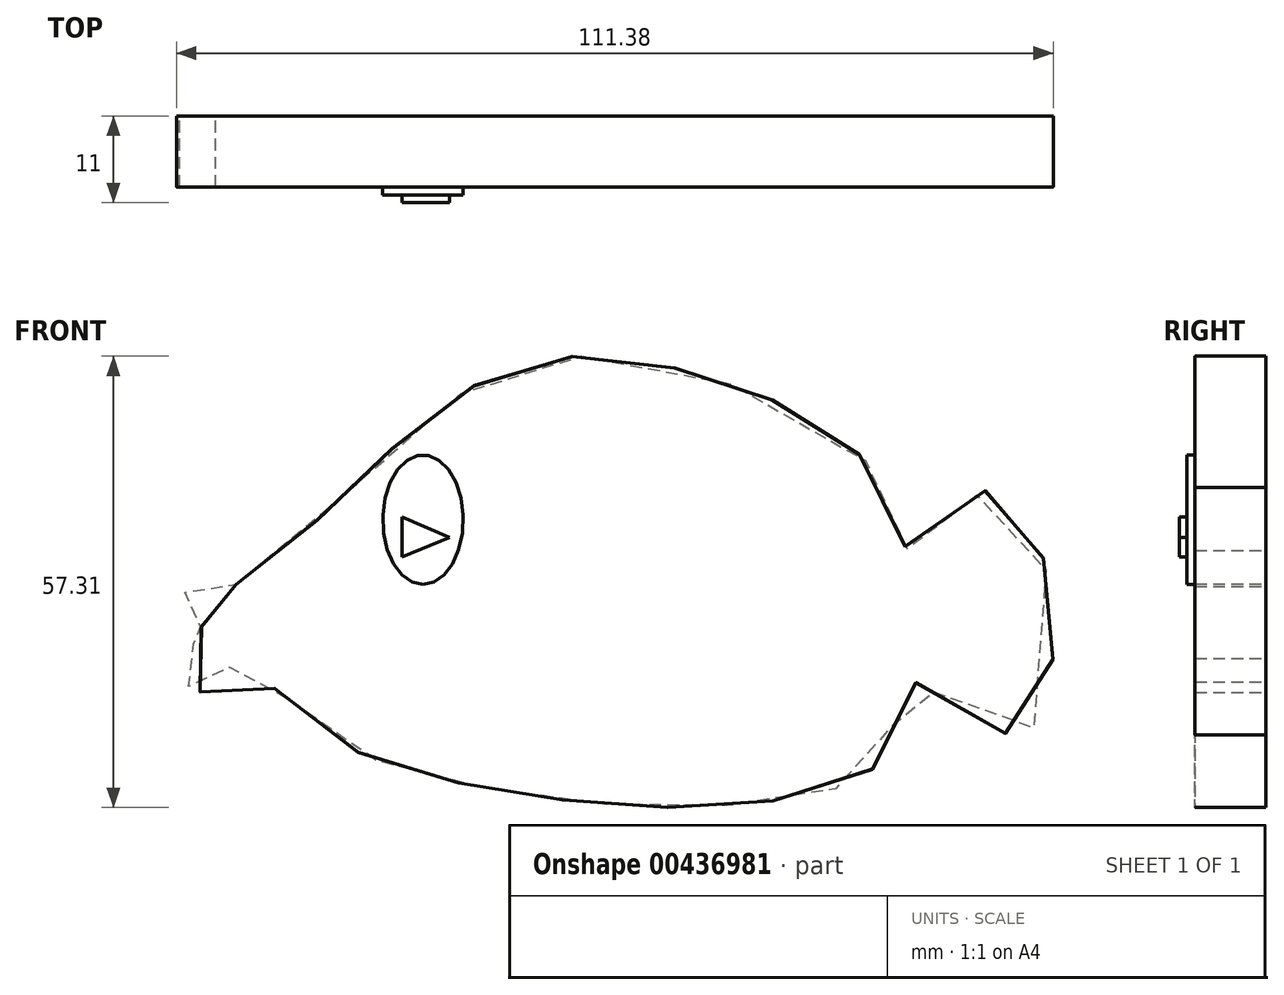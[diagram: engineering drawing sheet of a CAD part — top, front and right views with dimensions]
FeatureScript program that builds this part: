
annotation { "Feature Type Name" : "Feature", "Feature Type Description" : "" }
export const myFeature = defineFeature(function(context is Context, id is Id, definition is map)
    precondition{}
    {
        {
            var Q0;
            Q0=qCreatedBy(makeId("Front.planeOp"),FACE);
            var sketch = newSketch(context, id + "F0", { "sketchPlane" : qUnion([Q0])});
            skFitSpline(sketch, "E0", {"points": [v(-50.37, 0) * mm, v(-24.75, 22.16) * mm, v(0, 28.5) * mm, v(31.66, 12.95) * mm, v(35.69, 4.32) * mm, v(47.49, 12.09) * mm, v(50.37, -18.7) * mm, v(35.11, -12.38) * mm, v(32.23, -21) * mm, v(21, -27.05) * mm, v(0, -28.2) * mm, v(-23.02, -25.04) * mm, v(-40, -18.13) * mm, v(-50.65, -9.5) * mm, v(-52.1, -12.95) * mm, v(-56.4, -12.95) * mm, v(-57.27, -8.92) * mm, v(-54.68, -7.2) * mm, v(-52.96, -6.33) * mm, v(-56.7, -4.6) * mm, v(-57.85, -2.3) * mm, v(-54.68, 0) * mm, v(-50.37, 0) * mm]});
            skSolve(sketch);
        }
        {
            var Q0;
            Q0=makeQuery(id+"F0.imprint","IMPRINT",FACE,{"disambiguationData":[TD([[makeQuery(id+"F0.imprint","IMPRINT",EDGE,{"derivedFrom":sQuery(id+"F0.wireOp",EDGE,"E0")}),-1.0]])]});
            extrude(context, id + "F1", {"entities" : qUnion([Q0]), "depth" : 9 * mm});
        }
        {
            var Q0;
            Q0=makeQuery(id+"F1.opExtrude","CAP_FACE",FACE,{"disambiguationData":[OSD([sQuery(id+"F0.wireOp",EDGE,"E0")])],"isStart":false});
            var sketch = newSketch(context, id + "F2", { "sketchPlane" : qUnion([Q0])});
            skEllipse(sketch, "E1", {"center": v(-26.63, 8.21) * mm, "majorRadius": 8.21 * mm, "minorRadius": 5.12 * mm, "majorAxis": v(0, -1)});
            skSolve(sketch);
        }
        {
            var Q0;
            Q0=makeQuery(id+"F2.imprint","IMPRINT",FACE,{"disambiguationData":[TD([[makeQuery(id+"F2.imprint","IMPRINT",EDGE,{"derivedFrom":sQuery(id+"F2.wireOp",EDGE,"E1")}),1.0]])]});
            extrude(context, id + "F3", {"entities" : qUnion([Q0]), "operationType" : NewBodyOperationType.ADD, "depth" : 1 * mm});
        }
        {
            var Q0;
            Q0=makeQuery(id+"F3.opExtrude","CAP_FACE",FACE,{"disambiguationData":[OSD([sQuery(id+"F2.wireOp",EDGE,"E1")])],"isStart":false});
            var sketch = newSketch(context, id + "F4", { "sketchPlane" : qUnion([Q0])});
            skLineSegment(sketch, "E2", {"start": v(-29.3, 8.55) * mm, "end": v(-29.3, 3.47) * mm});
            skLineSegment(sketch, "E3", {"start": v(-29.3, 3.47) * mm, "end": v(-23.26, 5.97) * mm});
            skLineSegment(sketch, "E4", {"start": v(-23.26, 5.97) * mm, "end": v(-29.3, 8.55) * mm});
            skSolve(sketch);
        }
        {
            var Q0;
            Q0=makeQuery(id+"F4.imprint","IMPRINT",FACE,{"disambiguationData":[TD([[makeQuery(id+"F4.imprint","IMPRINT",EDGE,{"derivedFrom":sQuery(id+"F4.wireOp",EDGE,"E2")}),1.0]])]});
            extrude(context, id + "F5", {"entities" : qUnion([Q0]), "operationType" : NewBodyOperationType.ADD, "depth" : 1 * mm});
        }
        {
            var Q0;
            Q0=makeQuery(id+"F1.opExtrude","CAP_EDGE",EDGE,{"disambiguationData":[OSD([sQuery(id+"F0.wireOp",EDGE,"E0")])],"isStart":false});
            fillet(context, id + "F6", {"entities" : qUnion([Q0]), "radius" : 0.02 * mm, "tangentPropagation" : true, "allowEdgeOverflow" : false});
        }
    });
